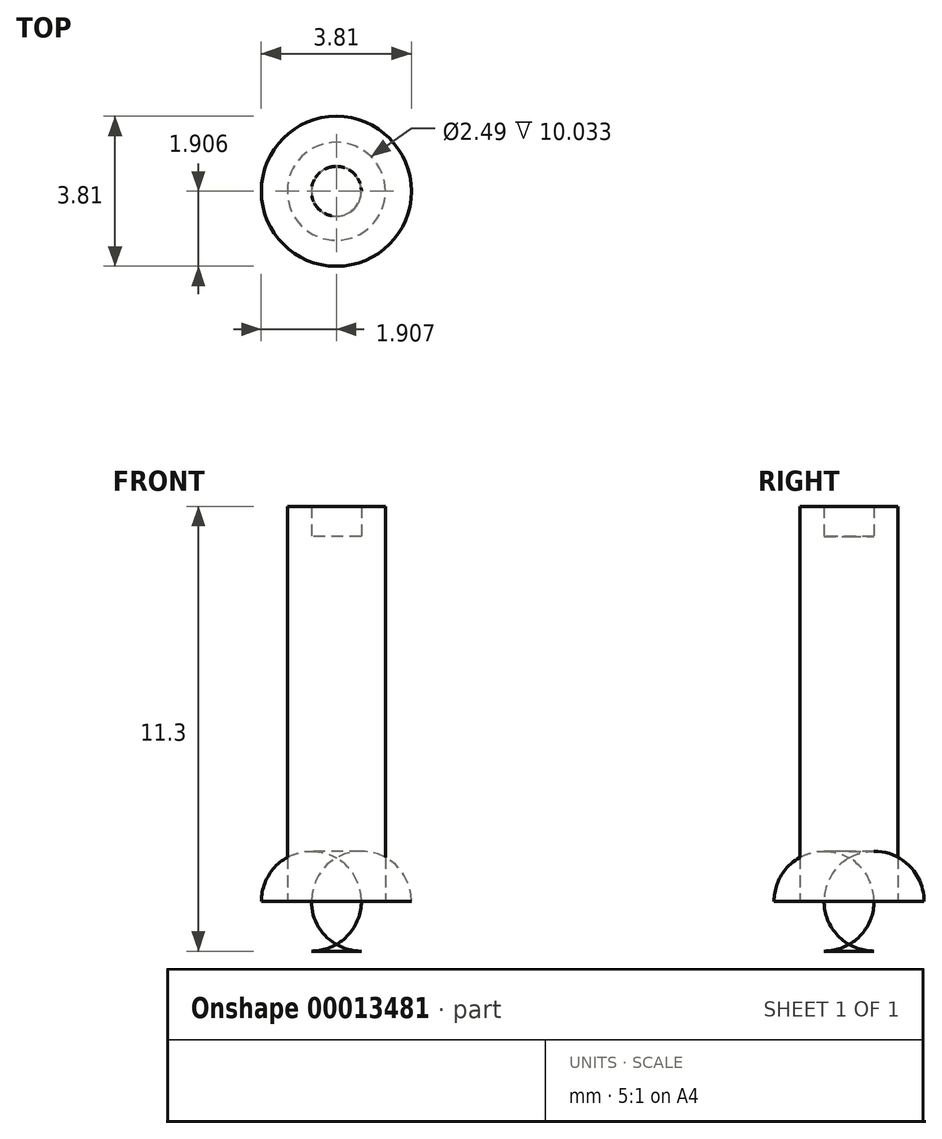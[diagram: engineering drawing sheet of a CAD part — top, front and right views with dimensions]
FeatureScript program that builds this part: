
annotation { "Feature Type Name" : "Feature", "Feature Type Description" : "" }
export const myFeature = defineFeature(function(context is Context, id is Id, definition is map)
    precondition{}
    {
        {
            var Q0;
            Q0=qCreatedBy(makeId("Top.planeOp"),FACE);
            var sketch = newSketch(context, id + "F0", { "sketchPlane" : qUnion([Q0])});
            skCircle(sketch, "E0", {"center": v(-42.71, -21.67) * mm, "radius": 1.9 * mm});
            skSolve(sketch);
        }
        {
            var Q0;
            Q0=makeQuery(id+"F0.imprint","IMPRINT",FACE,{"disambiguationData":[TD([[makeQuery(id+"F0.imprint","IMPRINT",EDGE,{"derivedFrom":sQuery(id+"F0.wireOp",EDGE,"E0")}),1.0]])]});
            extrude(context, id + "F1", {"entities" : qUnion([Q0]), "depth" : 1.27 * mm});
        }
        {
            var Q0;
            Q0=makeQuery(id+"F1.opExtrude","CAP_FACE",FACE,{"disambiguationData":[OSD([sQuery(id+"F0.wireOp",EDGE,"E0")])],"isStart":false});
            var sketch = newSketch(context, id + "F2", { "sketchPlane" : qUnion([Q0])});
            skCircle(sketch, "E1", {"center": v(-42.71, -21.67) * mm, "radius": 1.24 * mm});
            skSolve(sketch);
        }
        {
            var Q0;
            Q0=makeQuery(id+"F2.imprint","IMPRINT",FACE,{"disambiguationData":[TD([[makeQuery(id+"F2.imprint","IMPRINT",EDGE,{"derivedFrom":sQuery(id+"F2.wireOp",EDGE,"E1")}),1.0]])]});
            extrude(context, id + "F3", {"entities" : qUnion([Q0]), "operationType" : NewBodyOperationType.ADD, "depth" : 9.27 * mm});
        }
        {
            var Q0;
            Q0=makeQuery(id+"F3.opExtrude","CAP_FACE",FACE,{"disambiguationData":[OSD([sQuery(id+"F2.wireOp",EDGE,"E1")])],"isStart":false});
            var sketch = newSketch(context, id + "F4", { "sketchPlane" : qUnion([Q0])});
            skCircle(sketch, "E2", {"center": v(-42.71, -21.67) * mm, "radius": 1.24 * mm});
            skCircle(sketch, "E3", {"center": v(-42.71, -21.67) * mm, "radius": 0.64 * mm});
            skSolve(sketch);
        }
        {
            var Q0;
            Q0=makeQuery(id+"F4.imprint","IMPRINT",FACE,{"disambiguationData":[TD([[makeQuery(id+"F4.imprint","IMPRINT",EDGE,{"derivedFrom":sQuery(id+"F4.wireOp",EDGE,"E2")}),1.0]])]});
            extrude(context, id + "F5", {"entities" : qUnion([Q0]), "operationType" : NewBodyOperationType.ADD, "depth" : 0.76 * mm});
        }
        {
            var Q0;
            Q0=makeQuery(id+"F1.opExtrude","CAP_EDGE",EDGE,{"disambiguationData":[OSD([sQuery(id+"F0.wireOp",EDGE,"E0")])],"isStart":true});
            fillet(context, id + "F6", {"entities" : qUnion([Q0]), "radius" : 1.27 * mm, "tangentPropagation" : true, "allowEdgeOverflow" : false});
        }
    });
